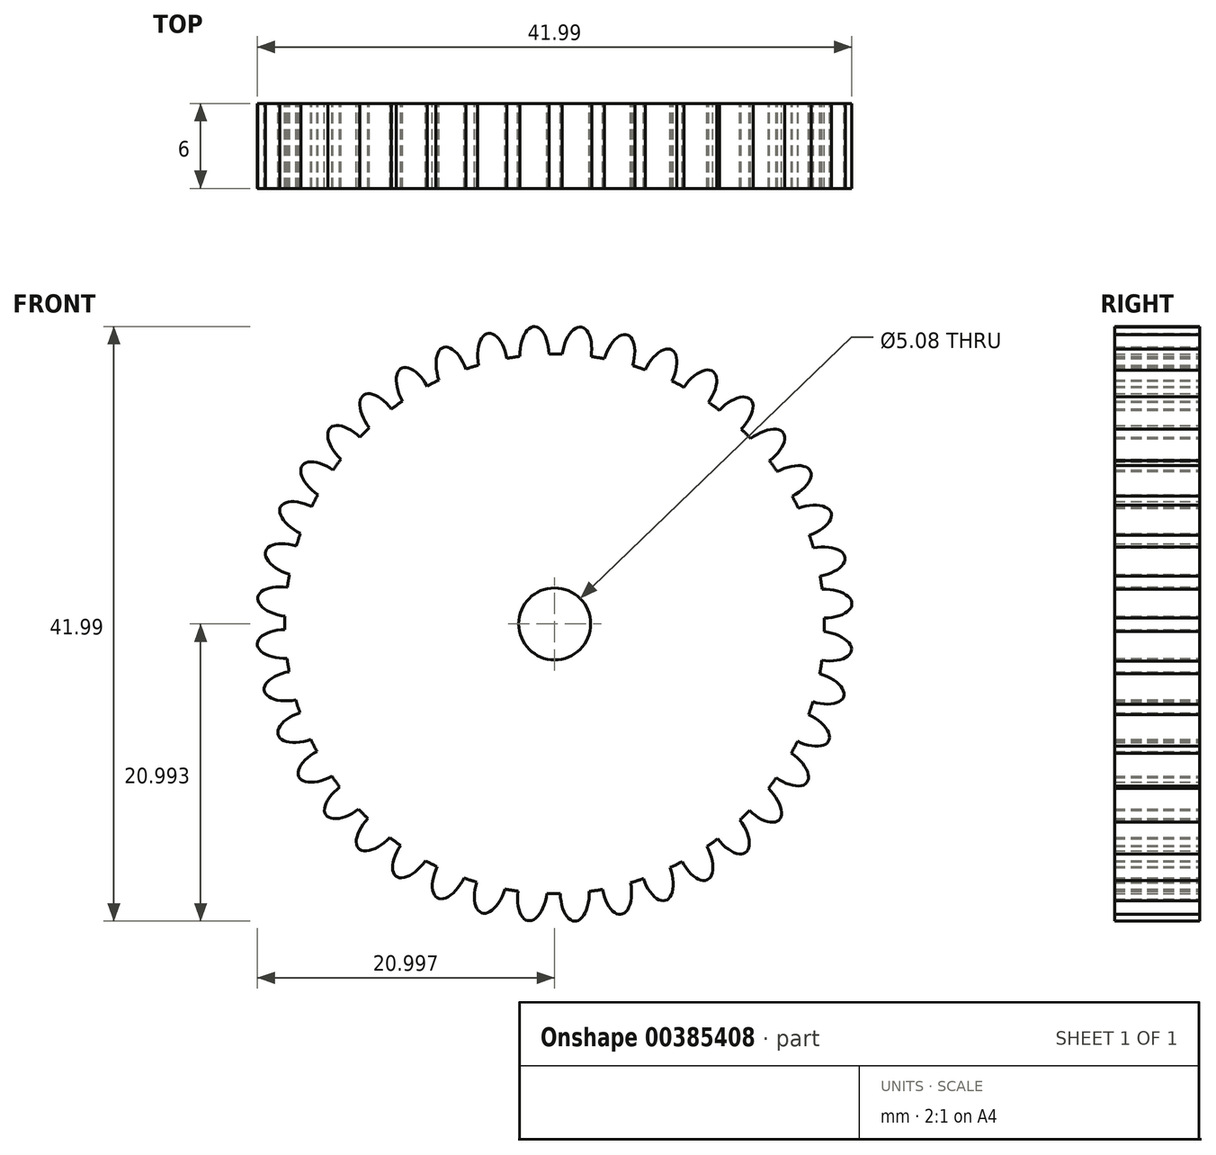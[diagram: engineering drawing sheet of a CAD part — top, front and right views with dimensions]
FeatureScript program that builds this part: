
annotation { "Feature Type Name" : "Feature", "Feature Type Description" : "" }
export const myFeature = defineFeature(function(context is Context, id is Id, definition is map)
    precondition{}
    {
        {
            var Q0;
            Q0=qCreatedBy(makeId("Front.planeOp"),FACE);
            var sketch = newSketch(context, id + "F0", { "sketchPlane" : qUnion([Q0])});
            skCircle(sketch, "E0", {"center": v(-9.97, 14.88) * mm, "radius": 19.05 * mm});
            skLineSegment(sketch, "E1", {"start": v(-9.97, 14.88) * mm, "end": v(-12.42, 33.78) * mm});
            skLineSegment(sketch, "E2", {"start": v(-9.97, 14.88) * mm, "end": v(-9.43, 33.93) * mm});
            skEllipticalArc(sketch, "E3", {});
            skEllipticalArc(sketch, "E4.1.0", {});
            skEllipticalArc(sketch, "E4.2.0", {});
            skEllipticalArc(sketch, "E4.3.0", {});
            skEllipticalArc(sketch, "E4.4.0", {});
            skEllipticalArc(sketch, "E4.5.0", {});
            skEllipticalArc(sketch, "E4.6.0", {});
            skEllipticalArc(sketch, "E4.7.0", {});
            skEllipticalArc(sketch, "E4.8.0", {});
            skEllipticalArc(sketch, "E4.9.0", {});
            skEllipticalArc(sketch, "E4.10.0", {});
            skEllipticalArc(sketch, "E4.11.0", {});
            skEllipticalArc(sketch, "E4.12.0", {});
            skEllipticalArc(sketch, "E4.13.0", {});
            skEllipticalArc(sketch, "E4.14.0", {});
            skEllipticalArc(sketch, "E4.15.0", {});
            skEllipticalArc(sketch, "E4.16.0", {});
            skEllipticalArc(sketch, "E4.17.0", {});
            skEllipticalArc(sketch, "E4.18.0", {});
            skEllipticalArc(sketch, "E4.19.0", {});
            skEllipticalArc(sketch, "E4.20.0", {});
            skEllipticalArc(sketch, "E4.21.0", {});
            skEllipticalArc(sketch, "E4.22.0", {});
            skEllipticalArc(sketch, "E4.23.0", {});
            skEllipticalArc(sketch, "E4.24.0", {});
            skEllipticalArc(sketch, "E4.25.0", {});
            skEllipticalArc(sketch, "E4.26.0", {});
            skEllipticalArc(sketch, "E4.27.0", {});
            skEllipticalArc(sketch, "E4.28.0", {});
            skEllipticalArc(sketch, "E4.29.0", {});
            skEllipticalArc(sketch, "E4.30.0", {});
            skEllipticalArc(sketch, "E4.31.0", {});
            skEllipticalArc(sketch, "E4.32.0", {});
            skEllipticalArc(sketch, "E4.33.0", {});
            skEllipticalArc(sketch, "E4.34.0", {});
            skEllipticalArc(sketch, "E4.35.0", {});
            skEllipticalArc(sketch, "E4.36.0", {});
            skEllipticalArc(sketch, "E4.37.0", {});
            skEllipticalArc(sketch, "E4.38.0", {});
            skEllipticalArc(sketch, "E4.39.0", {});
            skCircle(sketch, "E5", {"center": v(-9.97, 14.88) * mm, "radius": 2.54 * mm});
            const initialGuessF0  = {"E3": [-0.011399729166079028, 0.03387939530400499, 0, -1, 0.0019970374462838095, 0.001020793009534155, 1.595411977370606, 4.764581646804509], "E4.1.0": [-0.014353878070699497, 0.033422374293901776, 0.15643446504023098, -0.9876883405951378, 0.0019970374462838095, 0.001020793009534155, 1.595411977370606, 4.764581646804509], "E4.2.0": [-0.017200162662947386, 0.03250884926727232, 0.3090169943749475, -0.9510565162951535, 0.0019970374462838095, 0.001020793009534155, 1.595411977370606, 4.764581646804509], "E4.3.0": [-0.01986849796988457, 0.03116131424208802, 0.45399049973954686, -0.8910065241883678, 0.0019970374462838095, 0.001020793009534155, 1.595411977370606, 4.764581646804509], "E4.4.0": [-0.022293180720557103, 0.029412950002881216, 0.5877852522924732, -0.8090169943749473, 0.0019970374462838095, 0.001020793009534155, 1.595411977370606, 4.764581646804509], "E4.5.0": [-0.02441450717858272, 0.027306807079709436, 0.7071067811865476, -0.7071067811865475, 0.0019970374462838095, 0.001020793009534155, 1.595411977370606, 4.764581646804509], "E4.6.0": [-0.02618024324628595, 0.024894745701228783, 0.8090169943749476, -0.587785252292473, 0.0019970374462838095, 0.001020793009534155, 1.595411977370606, 4.764581646804509], "E4.7.0": [-0.027546910641537924, 0.022236158823750213, 0.8910065241883679, -0.4539904997395467, 0.0019970374462838095, 0.001020793009534155, 1.595411977370606, 4.764581646804509], "E4.8.0": [-0.028480857477358474, 0.019396509679541228, 0.9510565162951538, -0.3090169943749474, 0.0019970374462838095, 0.001020793009534155, 1.595411977370606, 4.764581646804509], "E4.9.0": [-0.028959086883057882, 0.016445719854787443, 0.9876883405951378, -0.1564344650402308, 0.0019970374462838095, 0.001020793009534155, 1.595411977370606, 4.764581646804509], "E4.10.0": [-0.028969823263515417, 0.013456447588084269, 1, 0, 0.0019970374462838095, 0.001020793009534155, 1.595411977370606, 4.764581646804509], "E4.11.0": [-0.0285128022534122, 0.010502298683463803, 0.9876883405951378, 0.1564344650402307, 0.0019970374462838095, 0.001020793009534155, 1.595411977370606, 4.764581646804509], "E4.12.0": [-0.02759927722678276, 0.007656014091215909, 0.9510565162951536, 0.30901699437494745, 0.0019970374462838095, 0.001020793009534155, 1.595411977370606, 4.764581646804509], "E4.13.0": [-0.026251742201598448, 0.004987678784278721, 0.891006524188368, 0.4539904997395469, 0.0019970374462838095, 0.001020793009534155, 1.595411977370606, 4.764581646804509], "E4.14.0": [-0.024503377962391645, 0.002562996033606199, 0.8090169943749476, 0.5877852522924732, 0.001997037446283809, 0.0010207930095341548, 1.595411977370606, 4.764581646804509], "E4.15.0": [-0.022397235039219865, 0.00044166957558057496, 0.7071067811865475, 0.7071067811865476, 0.0019970374462838095, 0.001020793009534155, 1.595411977370606, 4.764581646804509], "E4.16.0": [-0.019985173660739215, -0.0013240664921226539, 0.5877852522924731, 0.8090169943749475, 0.0019970374462838095, 0.001020793009534155, 1.595411977370606, 4.764581646804509], "E4.17.0": [-0.017326586783260642, -0.002690733887374626, 0.45399049973954675, 0.8910065241883679, 0.0019970374462838095, 0.001020793009534155, 1.595411977370606, 4.764581646804509], "E4.18.0": [-0.014486937639051655, -0.0036246807231951755, 0.30901699437494745, 0.9510565162951538, 0.0019970374462838095, 0.001020793009534155, 1.595411977370606, 4.764581646804509], "E4.19.0": [-0.01153614781429787, -0.004102910128894591, 0.1564344650402309, 0.9876883405951379, 0.0019970374462838095, 0.001020793009534155, 1.595411977370606, 4.764581646804509], "E4.20.0": [-0.0085468755475947, -0.0041136465093521216, 0, 1, 0.0019970374462838095, 0.001020793009534155, 1.595411977370606, 4.764581646804509], "E4.21.0": [-0.005592726642974232, -0.0036566254992489063, -0.15643446504023084, 0.9876883405951378, 0.0019970374462838095, 0.001020793009534155, 1.595411977370606, 4.764581646804509], "E4.22.0": [-0.002746442050726345, -0.002743100472619473, -0.309016994374947, 0.9510565162951538, 0.0019970374462838095, 0.001020793009534155, 1.595411977370606, 4.764581646804509], "E4.23.0": [-7.810674378914972e-05, -0.0013955654474351528, -0.4539904997395469, 0.891006524188368, 0.0019970374462838095, 0.001020793009534155, 1.595411977370606, 4.764581646804509], "E4.24.0": [0.0023465760068833753, 0.00035279879177164963, -0.5877852522924731, 0.8090169943749475, 0.0019970374462838095, 0.001020793009534155, 1.595411977370606, 4.764581646804509], "E4.25.0": [0.0044679024649089925, 0.0024589417149434266, -0.7071067811865476, 0.7071067811865476, 0.0019970374462838095, 0.001020793009534155, 1.595411977370606, 4.764581646804509], "E4.26.0": [0.006233638532612225, 0.00487100309342408, -0.8090169943749475, 0.5877852522924731, 0.0019970374462838095, 0.001020793009534155, 1.595411977370606, 4.764581646804509], "E4.27.0": [0.007600305927864197, 0.007529589970902651, -0.8910065241883679, 0.4539904997395468, 0.0019970374462838095, 0.001020793009534155, 1.595411977370606, 4.764581646804509], "E4.28.0": [0.008534252763684757, 0.01036923911511164, -0.9510565162951538, 0.3090169943749475, 0.0019970374462838095, 0.001020793009534155, 1.595411977370606, 4.764581646804509], "E4.29.0": [0.009012482169384165, 0.013320028939865423, -0.9876883405951379, 0.15643446504023095, 0.001997037446283809, 0.0010207930095341548, 1.595411977370606, 4.764581646804509], "E4.30.0": [0.009023218549841693, 0.016309301206568594, -1, 0, 0.0019970374462838095, 0.001020793009534155, 1.595411977370606, 4.764581646804509], "E4.31.0": [0.008566197539738477, 0.019263450111189063, -0.9876883405951378, -0.15643446504023079, 0.0019970374462838095, 0.001020793009534155, 1.595411977370606, 4.764581646804509], "E4.32.0": [0.007652672513109037, 0.022109734703436953, -0.9510565162951536, -0.30901699437494734, 0.0019970374462838095, 0.001020793009534155, 1.595411977370606, 4.764581646804509], "E4.33.0": [0.006305137487924724, 0.024778070010374145, -0.891006524188368, -0.45399049973954686, 0.0019970374462838095, 0.001020793009534155, 1.595411977370606, 4.764581646804509], "E4.34.0": [0.004556773248717921, 0.027202752761046667, -0.8090169943749477, -0.5877852522924731, 0.0019970374462838095, 0.001020793009534155, 1.595411977370606, 4.764581646804509], "E4.35.0": [0.0024506303255461444, 0.029324079219072284, -0.7071067811865476, -0.7071067811865475, 0.0019970374462838095, 0.001020793009534155, 1.595411977370606, 4.764581646804509], "E4.36.0": [3.856894706549298e-05, 0.03108981528677552, -0.5877852522924732, -0.8090169943749475, 0.0019970374462838095, 0.001020793009534155, 1.595411977370606, 4.764581646804509], "E4.37.0": [-0.0026200179304130787, 0.03245648268202749, -0.45399049973954686, -0.8910065241883679, 0.0019970374462838095, 0.001020793009534155, 1.595411977370606, 4.764581646804509], "E4.38.0": [-0.005459667074622067, 0.03339042951784805, -0.3090169943749475, -0.9510565162951535, 0.0019970374462838095, 0.001020793009534155, 1.595411977370606, 4.764581646804509], "E4.39.0": [-0.00841045689937585, 0.03386865892354746, -0.156434465040231, -0.9876883405951379, 0.0019970374462838095, 0.001020793009534155, 1.595411977370606, 4.764581646804509]};
            skSetInitialGuess(sketch, initialGuessF0);
            skSolve(sketch);
        }
        {
            var Q0;
            Q0=qSketchRegion(id+"F0",true);
            extrude(context, id + "F1", {"entities" : qUnion([Q0]), "depth" : 6 * mm});
        }
    });
